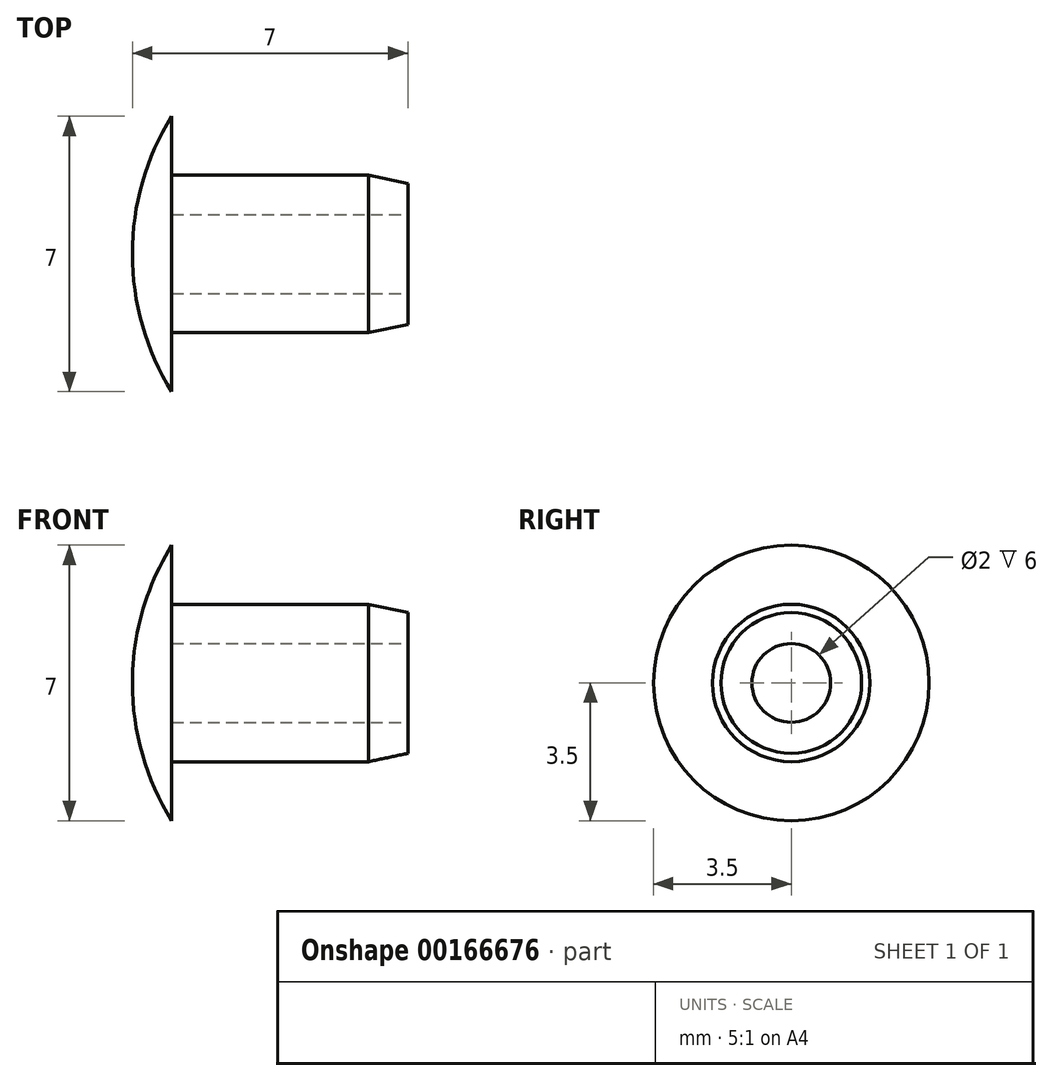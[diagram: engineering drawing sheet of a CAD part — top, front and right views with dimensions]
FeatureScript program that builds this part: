
annotation { "Feature Type Name" : "Feature", "Feature Type Description" : "" }
export const myFeature = defineFeature(function(context is Context, id is Id, definition is map)
    precondition{}
    {
        {
            var Q0;
            Q0=qCreatedBy(makeId("Front.planeOp"),FACE);
            var sketch = newSketch(context, id + "F0", { "sketchPlane" : qUnion([Q0])});
            skLineSegment(sketch, "E0", {"start": v(0, 0) * mm, "end": v(-82.14, 0) * mm, "construction": true});
            skLineSegment(sketch, "E1", {"start": v(1, 3.5) * mm, "end": v(1, 2) * mm});
            skLineSegment(sketch, "E2", {"start": v(1, 2) * mm, "end": v(6, 2) * mm});
            skLineSegment(sketch, "E3", {"start": v(6, 2) * mm, "end": v(7, 1.79) * mm});
            skLineSegment(sketch, "E4", {"start": v(7, 1.79) * mm, "end": v(7, 1) * mm});
            skLineSegment(sketch, "E5", {"start": v(7, 1) * mm, "end": v(1, 1) * mm});
            skLineSegment(sketch, "E6", {"start": v(1, 1) * mm, "end": v(1, 0) * mm});
            skArc(sketch, "E7", {"start": v(1, 3.5) * mm, "mid": v(0.25, 1.82) * mm, "end": v(0, 0) * mm});
            skLineSegment(sketch, "E8", {"start": v(0, 0) * mm, "end": v(1, 0) * mm});
            skSolve(sketch);
        }
        {
            var Q0;
            Q0=makeQuery(id+"F0.imprint","IMPRINT",FACE,{"disambiguationData":[TD([[makeQuery(id+"F0.imprint","IMPRINT",EDGE,{"derivedFrom":sQuery(id+"F0.wireOp",EDGE,"E1")}),-1.0]])]});
            var Q1;
            Q1=sQuery(id+"F0.wireOp",EDGE,"E0");
            revolve(context, id + "F1", {"entities" : qUnion([Q0]), "axis" : qUnion([Q1]), "revolveType" : RevolveType.FULL});
        }
    });
